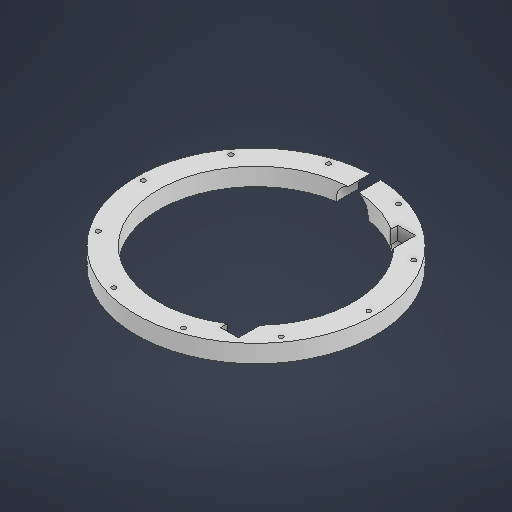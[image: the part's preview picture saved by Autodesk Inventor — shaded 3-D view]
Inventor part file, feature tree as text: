
AUTODESK INVENTOR PART (.ipt)
format: ipt  version: 2025 (Build 290162000, 162)  size: 259,584 bytes
history: native  units: in
note: dims shown in document units (in); Inventor stores cm internally (conversion verified against a paired STEP export)
features: sketch x6, extrude x4, hole x1
ambient origin geometry x8: Origin, YZ Plane, XZ Plane, XY Plane, X Axis, Y Axis, Z Axis, Center Point
bodies: Solid1 (feature_tree)
feature tree (11):
  extrude  "Extrusion1"  Depth=8.6614in
  extrude  "Extrusion2"  Depth=1.4173in
  hole  "Hole1"  [1 undecoded]
  extrude  "Extrusion3"  Depth=3.937in TaperAngle=360.0deg
  extrude  "Extrusion7"  Depth=0.3937in TaperAngle=0.0deg
  sketch  "Sketch1"  dims[d0=10.6299in d1=8.6614in]
  sketch  "Sketch2"  dims[d5=0.0in d6=0.0in d7=10.0394in]
  sketch  "Sketch3"  dims[d8=0.1575in d9=3.937in d11=360.0deg]
  sketch  "Sketch Circular Pattern1"  dims[d2=1.8504in d3=0.0in d4=1.4173in]
  sketch  "Sketch4"  dims[d13=0.1969in d14=0.3937in d15=0.1575in d16=0.0787in d17=90.0deg d18=0.5591in d19=0.8108in d20=1.063in d21=0.0in]
  sketch  "Sketch7"  dims[d38=0.1181in d39=2.7559in d40=0.7874in d41=7.874in d42=0.5906in d43=0.0in d30=0.0197in d31=0.0344in d32=0.0197in d33=0.0344in d44=0.5635in d45=0.0295in d46=0.8108in d47=0.0025in d48=0.0295in d49=0.0148in]
note: 1 required parameter value undecoded (feature->parameter linkage not recoverable at this tier; creation-order binding heuristic only, values carry confidence <= 0.55)
